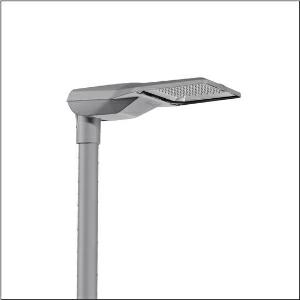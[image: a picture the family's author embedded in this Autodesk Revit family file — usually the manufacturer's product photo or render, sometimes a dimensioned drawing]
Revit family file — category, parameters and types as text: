
# Revit family: streetlight_sl_21_midi___pc-r_5xe7g33a08mb_1ce8
name_source: partatom
category: Lighting Fixtures
units: mm (PartAtom-declared; Revit-internal decimal feet)

## family parameters
Cut with Voids When Loaded = No
Host = Face
Light Source = No
Part Type = Normal
Room Calculation Point = No
Round Connector Dimension = Use Diameter
Shared = No

## types (1)
- --- (1 x LED, 17390 lm, 136 W, 3000K)
    Apparent Load = 136 VA
    CIE Flux Codes = 38 78 98 100 100
    Color Rendering = 70
    Color Temperature = 3000K
    Default Elevation = 1800 mm
    Description = Streetlight SL 21 midi, mast luminaire, primary light control with lens, of PMMA, primary optical cover: cover, of toughened safety glass, transparent, light distribution: PC-R, light emission: direct distribution, primary light characteristic: asymmetric, right, installation type: post-top, side-entry, LED, 3G 1.5mm², High Power LED, rated luminous flux: 17.390lm, luminous efficacy: 128lm/W, light colour: 730, colour temperature: 3000K, control: overheat protection, constant luminous flux control, time-dependent luminous flux control, flexible luminous flux parameterisation, mains connection: 220..240V, AC, 50/60Hz, connection cable pre-assembled, cable length: 12,5m, wiring characteristics: H07RN-F, start of lifetime: 136W, end of service life: 142W, reduction: 61W, luminaire housing, of diecast aluminium, powder-coated, Siteco® metallic grey (DB 702S), corrosivity category C5 mid according to DIN EN ISO 12944, please order mast flange separately, inclination adjustable: 0°, 5°, 10°, 15°, sealing non-destructively replaceable, multi-level sealing system, length: 644mm, width: 335mm, height: 110mm, mast flange for spigot size: 42mm (side-entry): 5XC10008XM4, 60/48mm (side-entry/post-top): 5XC10108XM2, 76/60mm (side-entry/post-top): 5XC10108XM1, protection rating (complete): IP66, insulation class (complete): insulation class II (safety insulation), certification: CE, ENEC, ENEC+, VDE, impact resistance: IK09, permissible operating ambient temperature for outdoor applications: -40..+50°C, standard-compliant lighting for roads and squares, packaging unit: 1 piece

Light Distribution: PC-R
    Height = 111 mm
    Lamp = 1 x LED
    Lamp Light Flux = 17390 lm
    Lamp Power = 136 W
    Lamp count = 1
    Length = 644 mm
    Luminous efficacy = 128 lm/W
    Manufacturer = Siteco
    ModVariant = No
    Model = 5XE7G33A08MB
    Number of Poles = 1
    OnlyDefault = Yes
    Power Factor = 1
    Product Name = Streetlight SL 21 midi | PC-R
    Product group = mast luminaire | pylon top
    ProductGroupID = 6100
    Protection Class = Protection class II
    Protection Degree = IP 66
    RLX_Detail_Level = 1
    RLX_Emergency_Light_Flux = 0 lm
    RLX_Emergency_Type = 0
    RLX_Emergency_Type_DB = No
    RlxData = <blob elided: 92969 chars, md5=2fa13270>
    Socket = socket
    Standby Power = 0 W
    System Light Flux = 17390 lm
    System Power = 136 W
    Type Comments = factory setting: luminous flux: 100 % | Output Level: 100 % | 695 mA
    Type Image = l_1004298.jpg
    URL = http://relux.com
    VarID = @adj_022837
    Voltage = 0 V
    Weight = 0.00 kg
    Width = 336 mm

## geometry (parser evidence)
native form markers: Blend x4, Sweep x11
no freeform markers — native parametric forms only
